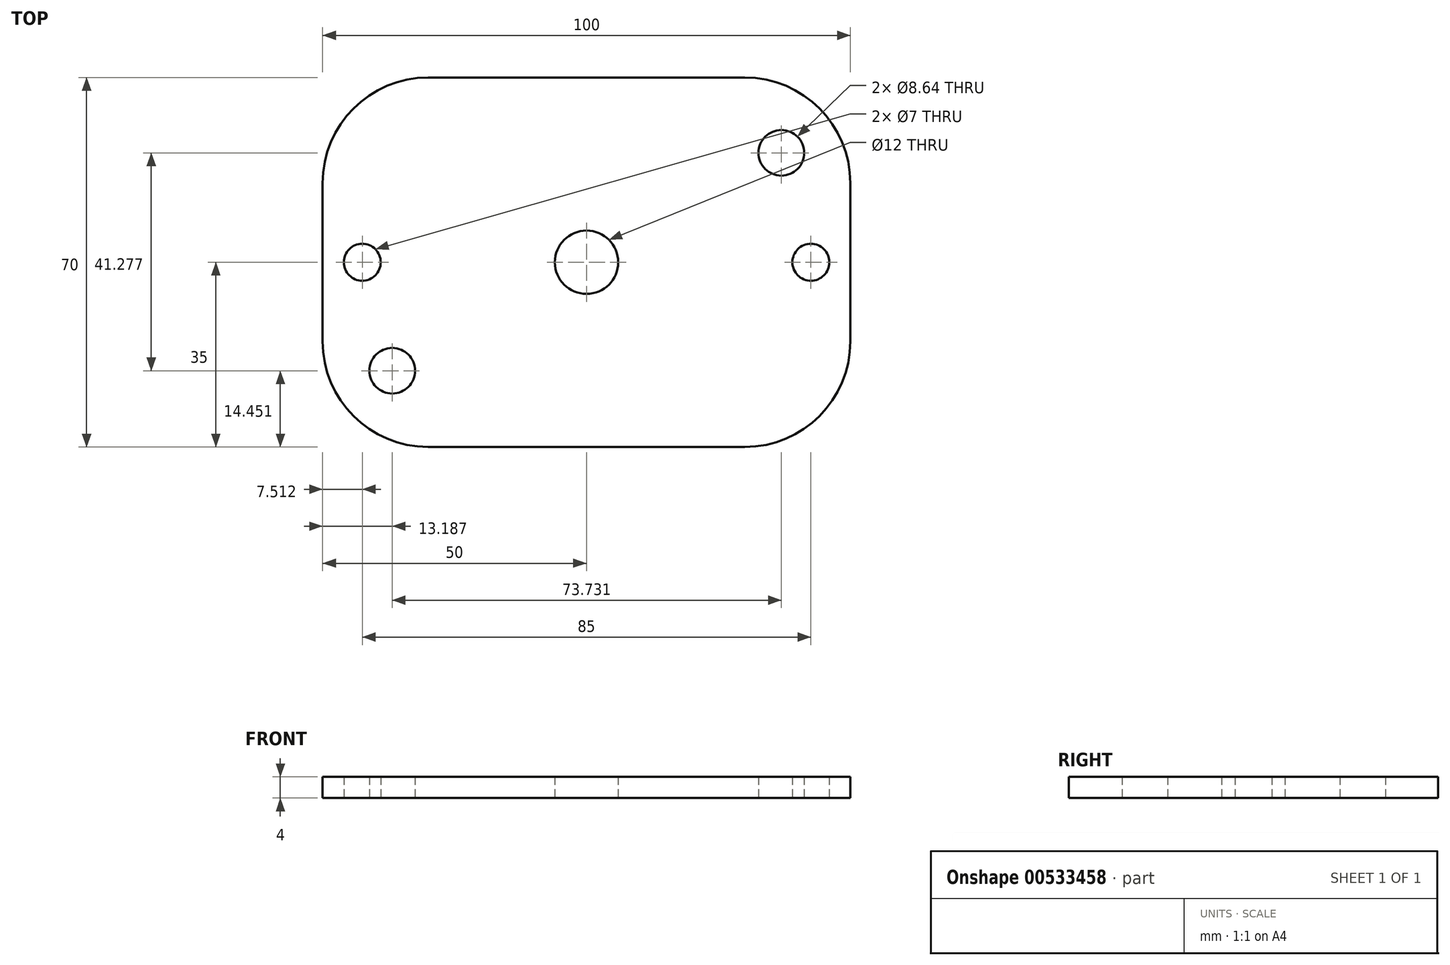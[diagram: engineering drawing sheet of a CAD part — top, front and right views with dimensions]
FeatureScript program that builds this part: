
annotation { "Feature Type Name" : "Feature", "Feature Type Description" : "" }
export const myFeature = defineFeature(function(context is Context, id is Id, definition is map)
    precondition{}
    {
        {
            var Q0;
            Q0=qCreatedBy(makeId("Top.planeOp"),FACE);
            var sketch = newSketch(context, id + "F0", { "sketchPlane" : qUnion([Q0])});
            skLineSegment(sketch, "E0.bottom", {"start": v(-50, 35) * mm, "end": v(50, 35) * mm});
            skLineSegment(sketch, "E0.top", {"start": v(-50, -35) * mm, "end": v(50, -35) * mm});
            skLineSegment(sketch, "E0.left", {"start": v(-50, 35) * mm, "end": v(-50, -35) * mm});
            skLineSegment(sketch, "E0.right", {"start": v(50, 35) * mm, "end": v(50, -35) * mm});
            skPoint(sketch, "E0.middle", {"position": v(0, 0) * mm});
            skSolve(sketch);
        }
        {
            var Q0;
            Q0=makeQuery(id+"F0.imprint","IMPRINT",FACE,{"disambiguationData":[TD([[makeQuery(id+"F0.imprint","IMPRINT",EDGE,{"derivedFrom":sQuery(id+"F0.wireOp",EDGE,"E0.bottom")}),-1.0]])]});
            var sketch = newSketch(context, id + "F1", { "sketchPlane" : qUnion([Q0])});
            skCircle(sketch, "E1", {"center": v(-42.49, 0) * mm, "radius": 3.5 * mm});
            skCircle(sketch, "E2.MirrorC", {"center": v(42.51, 0) * mm, "radius": 3.5 * mm});
            skSolve(sketch);
        }
        {
            var Q0;
            Q0=qCreatedBy(makeId("Top.planeOp"),FACE);
            var sketch = newSketch(context, id + "F2", { "sketchPlane" : qUnion([Q0])});
            skCircle(sketch, "E3.MirrorC", {"center": v(36.92, 20.73) * mm, "radius": 4.32 * mm});
            skCircle(sketch, "E4.MirrorC", {"center": v(-36.81, -20.55) * mm, "radius": 4.32 * mm});
            skSolve(sketch);
        }
        {
            var Q0;
            Q0=makeQuery(id+"F0.imprint","IMPRINT",FACE,{"disambiguationData":[TD([[makeQuery(id+"F0.imprint","IMPRINT",EDGE,{"derivedFrom":sQuery(id+"F0.wireOp",EDGE,"E0.bottom")}),-1.0]])]});
            extrude(context, id + "F3", {"entities" : qUnion([Q0]), "depth" : 4 * mm, "offsetDistance" : 25 * mm});
        }
        {
            var Q0;
            Q0 = qSketchRegion(id + "F2", true);
            extrude(context, id + "F4", {"entities" : qUnion([Q0]), "operationType" : NewBodyOperationType.REMOVE, "depth" : 5 * mm, "offsetDistance" : 25 * mm});
        }
        {
            var Q0;
            Q0 = qSketchRegion(id + "F1", true);
            extrude(context, id + "F5", {"entities" : qUnion([Q0]), "operationType" : NewBodyOperationType.REMOVE, "depth" : 5 * mm, "offsetDistance" : 25 * mm});
        }
        {
            var Q0;
            Q0=makeQuery(id+"F3.opExtrude","SWEPT_EDGE",EDGE,{"disambiguationData":[OSD([sQuery(id+"F0.wireOp",EDGE,"E0.top"),sQuery(id+"F0.wireOp",EDGE,"E0.left")])]});
            fillet(context, id + "F6", {"entities" : qUnion([Q0]), "radius" : 20 * mm, "tangentPropagation" : true, "allowEdgeOverflow" : false});
        }
        {
            var Q0;
            Q0=makeQuery(id+"F3.opExtrude","SWEPT_EDGE",EDGE,{"disambiguationData":[OSD([sQuery(id+"F0.wireOp",EDGE,"E0.bottom"),sQuery(id+"F0.wireOp",EDGE,"E0.right")])]});
            fillet(context, id + "F7", {"entities" : qUnion([Q0]), "radius" : 20 * mm, "tangentPropagation" : true, "allowEdgeOverflow" : false});
        }
        {
            var Q0;
            Q0=makeQuery(id+"F3.opExtrude","SWEPT_EDGE",EDGE,{"disambiguationData":[OSD([sQuery(id+"F0.wireOp",EDGE,"E0.top"),sQuery(id+"F0.wireOp",EDGE,"E0.right")])]});
            fillet(context, id + "F8", {"entities" : qUnion([Q0]), "radius" : 20 * mm, "tangentPropagation" : true, "allowEdgeOverflow" : false});
        }
        {
            var Q0;
            Q0=makeQuery(id+"F3.opExtrude","SWEPT_EDGE",EDGE,{"disambiguationData":[OSD([sQuery(id+"F0.wireOp",EDGE,"E0.bottom"),sQuery(id+"F0.wireOp",EDGE,"E0.left")])]});
            fillet(context, id + "F9", {"entities" : qUnion([Q0]), "radius" : 20 * mm, "tangentPropagation" : true, "allowEdgeOverflow" : false});
        }
        {
            var Q0;
            Q0=makeQuery(id+"F3.opExtrude","CAP_FACE",FACE,{"disambiguationData":[OSD([sQuery(id+"F0.wireOp",EDGE,"E0.bottom"),sQuery(id+"F0.wireOp",EDGE,"E0.top"),sQuery(id+"F0.wireOp",EDGE,"E0.left"),sQuery(id+"F0.wireOp",EDGE,"E0.right")])],"isStart":true});
            var sketch = newSketch(context, id + "F10", { "sketchPlane" : qUnion([Q0])});
            skCircle(sketch, "E5", {"center": v(0, 0) * mm, "radius": 6 * mm});
            skSolve(sketch);
        }
        {
            var Q0;
            Q0 = qSketchRegion(id + "F10", true);
            extrude(context, id + "F11", {"entities" : qUnion([Q0]), "operationType" : NewBodyOperationType.REMOVE, "oppositeDirection" : true, "depth" : 5 * mm, "offsetDistance" : 25 * mm});
        }
    });
